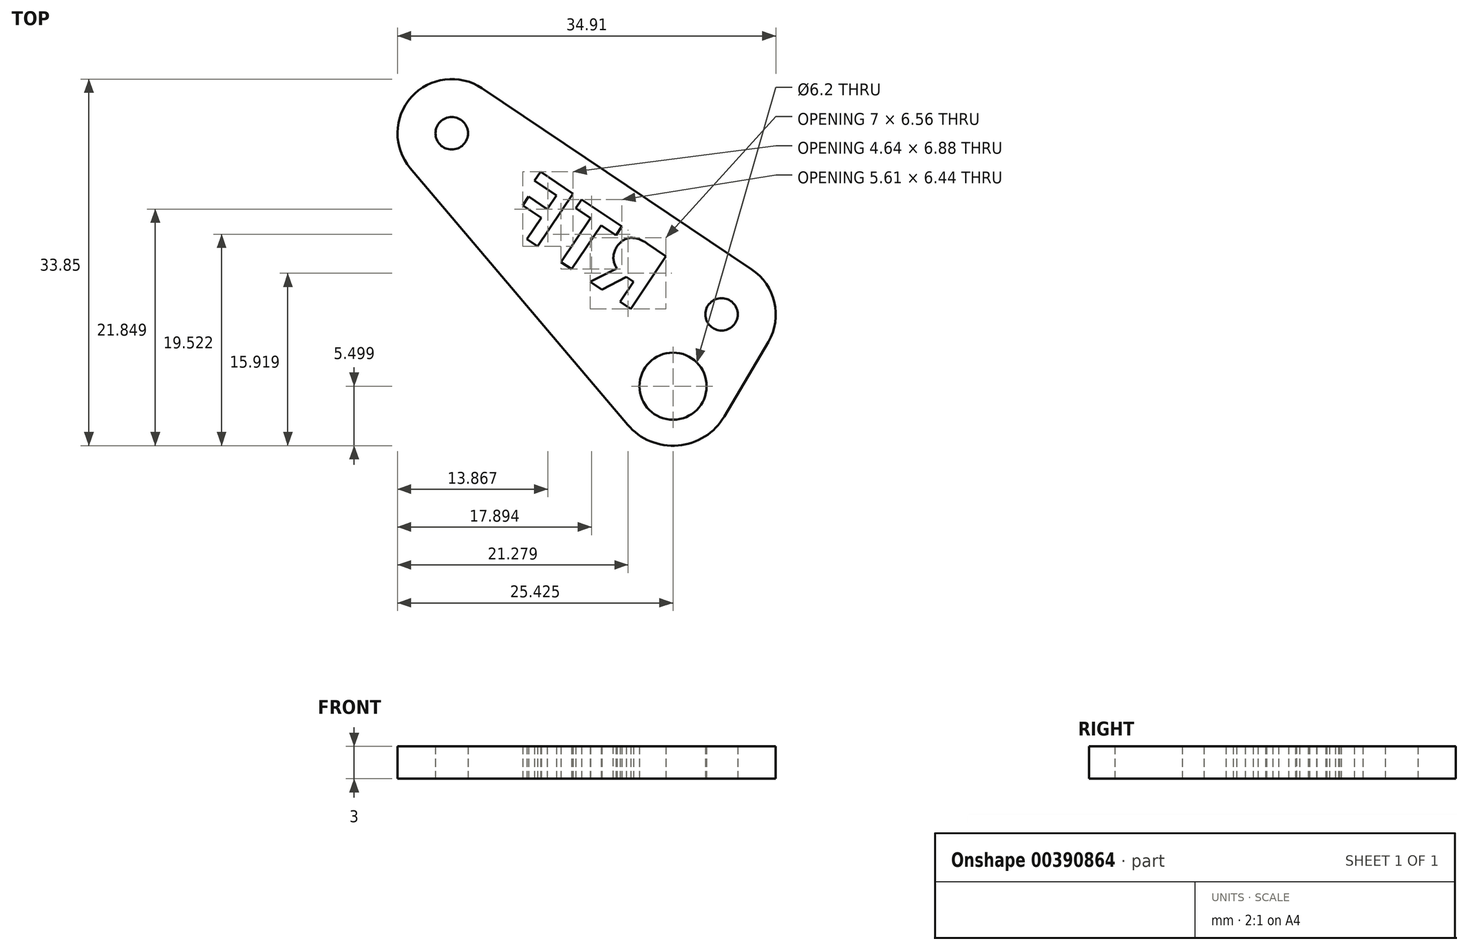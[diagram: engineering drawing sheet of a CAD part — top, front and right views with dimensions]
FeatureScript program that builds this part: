
annotation { "Feature Type Name" : "Feature", "Feature Type Description" : "" }
export const myFeature = defineFeature(function(context is Context, id is Id, definition is map)
    precondition{}
    {
        {
            var Q0;
            Q0=qCreatedBy(makeId("Top.planeOp"),FACE);
            var sketch = newSketch(context, id + "F0", { "sketchPlane" : qUnion([Q0])});
            skPoint(sketch, "E0.middle", {"position": v(0, 0) * mm});
            skPoint(sketch, "E1.third.point", {"position": v(2.06, 0.94) * mm});
            skCircle(sketch, "E2", {"center": v(-2.43, -5.7) * mm, "radius": 3.1 * mm});
            skCircle(sketch, "E3", {"center": v(2.06, 0.94) * mm, "radius": 1.5 * mm});
            skLineSegment(sketch, "E4", {"start": v(2.06, 0.94) * mm, "end": v(-6.25, 6.51) * mm, "construction": true});
            skCircle(sketch, "E5", {"center": v(-22.85, 17.66) * mm, "radius": 1.5 * mm});
            skArc(sketch, "E6", {"start": v(-6.62, -9.24) * mm, "mid": v(-1.96, -11.17) * mm, "end": v(2.31, -8.48) * mm});
            skArc(sketch, "E7", {"start": v(-20.06, 21.81) * mm, "mid": v(-26.57, 21) * mm, "end": v(-26.66, 14.43) * mm});
            skLineSegment(sketch, "E8", {"start": v(6.36, -1.6) * mm, "end": v(2.31, -8.48) * mm});
            skLineSegment(sketch, "E9", {"start": v(2.06, 0.94) * mm, "end": v(-2.43, -5.7) * mm, "construction": true});
            skLineSegment(sketch, "E10", {"start": v(-2.43, -5.7) * mm, "end": v(-22.85, 17.66) * mm, "construction": true});
            skLineSegment(sketch, "E11", {"start": v(-6.62, -9.24) * mm, "end": v(-26.66, 14.43) * mm});
            skLineSegment(sketch, "E12", {"start": v(4.87, 5.07) * mm, "end": v(-20.06, 21.81) * mm});
            skArc(sketch, "E13.trimOffspring", {"start": v(6.36, -1.6) * mm, "mid": v(6.93, 2.06) * mm, "end": v(4.82, 5.1) * mm});
            skSolve(sketch);
        }
        {
            var Q0;
            Q0=qSketchRegion(id+"F0",true);
            extrude(context, id + "F1", {"entities" : qUnion([Q0]), "depth" : 3 * mm, "offsetDistance" : 25 * mm});
        }
        {
            var Q0;
            Q0=makeQuery(id+"F1.opExtrude","CAP_FACE",FACE,{"disambiguationData":[OSD([sQuery(id+"F0.wireOp",EDGE,"E2"),sQuery(id+"F0.wireOp",EDGE,"E3"),sQuery(id+"F0.wireOp",EDGE,"E5"),sQuery(id+"F0.wireOp",EDGE,"E6"),sQuery(id+"F0.wireOp",EDGE,"E7"),sQuery(id+"F0.wireOp",EDGE,"E8"),sQuery(id+"F0.wireOp",EDGE,"E11"),sQuery(id+"F0.wireOp",EDGE,"E12"),sQuery(id+"F0.wireOp",EDGE,"E13.trimOffspring")])],"isStart":true});
            var sketch = newSketch(context, id + "F2", { "sketchPlane" : qUnion([Q0])});
            skText(sketch, "E14", { "text": "RTF\n", "fontName": "NotoSansCJKsc-Bold.otf"});
            const initialGuessF2  = {"E14": [-0.00574, -0.00105, -0.83014, -0.55755, 0.0057]};
            skSetInitialGuess(sketch, initialGuessF2);
            skSolve(sketch);
        }
        {
            var Q0;
            Q0 = qSketchRegion(id + "F2", true);
            extrude(context, id + "F3", {"entities" : qUnion([Q0]), "operationType" : NewBodyOperationType.REMOVE, "oppositeDirection" : true, "depth" : 25 * mm, "offsetDistance" : 25 * mm});
        }
        {
            var Q0;
            Q0=makeQuery(id+"F3.boolean.opBoolean","SPLIT",FACE,{"disambiguationData":[TD([makeQuery(id+"F3.opExtrude","SWEPT_FACE",FACE,{"disambiguationData":[OSD([sQuery(id+"F2.wireOp",EDGE,"E14.sketch_text.stroke-0")])]})])],"derivedFrom":makeQuery(id+"F1.opExtrude","CAP_FACE",FACE,{"disambiguationData":[OSD([sQuery(id+"F0.wireOp",EDGE,"E2"),sQuery(id+"F0.wireOp",EDGE,"E3"),sQuery(id+"F0.wireOp",EDGE,"E5"),sQuery(id+"F0.wireOp",EDGE,"E6"),sQuery(id+"F0.wireOp",EDGE,"E7"),sQuery(id+"F0.wireOp",EDGE,"E8"),sQuery(id+"F0.wireOp",EDGE,"E11"),sQuery(id+"F0.wireOp",EDGE,"E12"),sQuery(id+"F0.wireOp",EDGE,"E13.trimOffspring")])],"isStart":true})});
            extrude(context, id + "F4", {"entities" : qUnion([Q0]), "operationType" : NewBodyOperationType.REMOVE, "oppositeDirection" : true, "depth" : 25 * mm, "offsetDistance" : 25 * mm});
        }
    });
